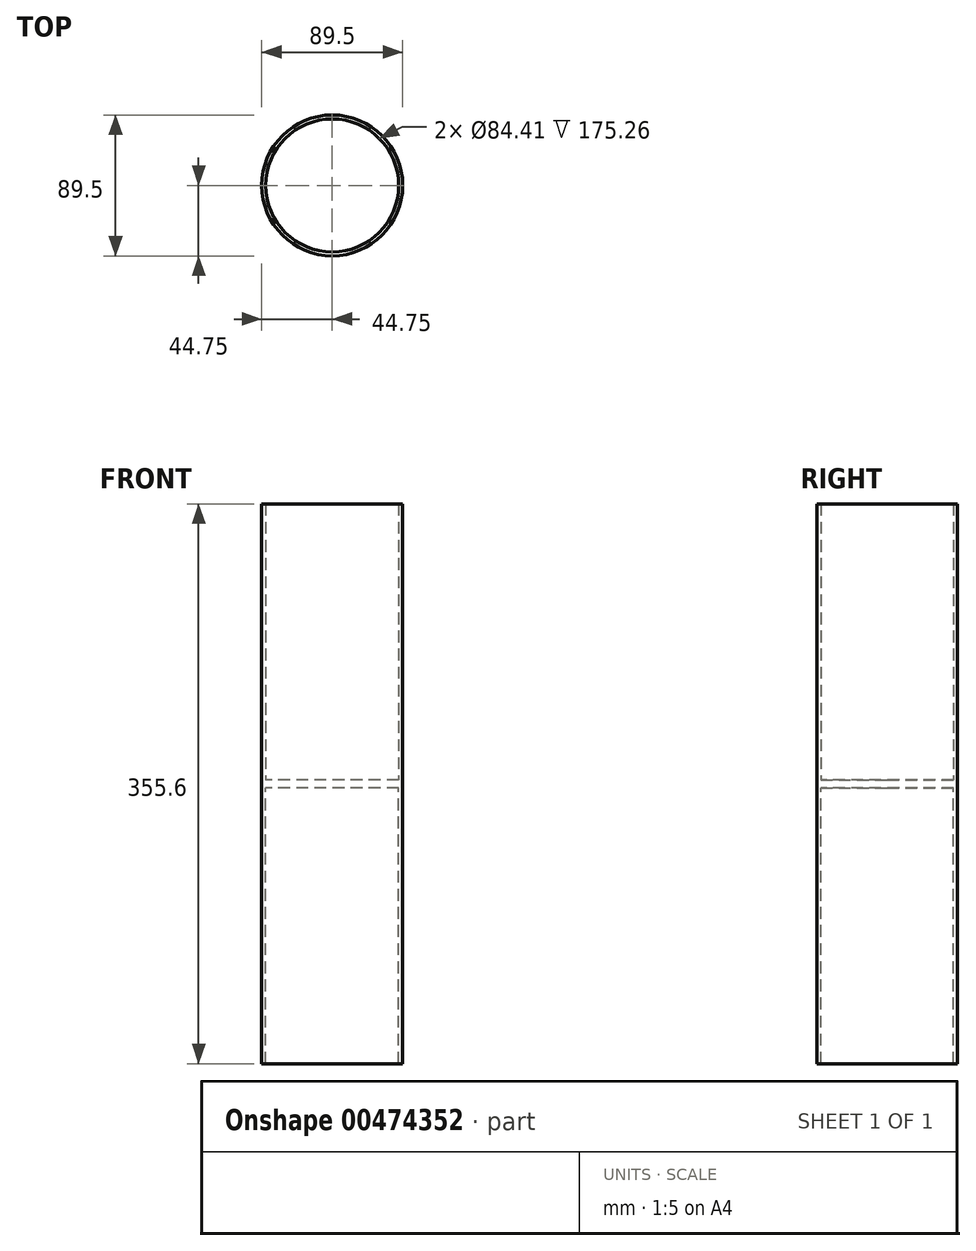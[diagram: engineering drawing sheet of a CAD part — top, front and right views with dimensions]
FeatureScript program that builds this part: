
annotation { "Feature Type Name" : "Feature", "Feature Type Description" : "" }
export const myFeature = defineFeature(function(context is Context, id is Id, definition is map)
    precondition{}
    {
        {
            var Q0;
            Q0=qCreatedBy(makeId("Top.planeOp"),FACE);
            var sketch = newSketch(context, id + "F0", { "sketchPlane" : qUnion([Q0])});
            skCircle(sketch, "E0", {"center": v(0, 0) * mm, "radius": 44.75 * mm});
            skSolve(sketch);
        }
        {
            var Q0;
            Q0 = qSketchRegion(id + "F0", true);
            extrude(context, id + "F1", {"entities" : qUnion([Q0]), "depth" : 177.8 * mm});
        }
        {
            var Q0;
            Q0=makeQuery(id+"F1.opExtrude","CAP_FACE",FACE,{"disambiguationData":[OSD([sQuery(id+"F0.wireOp",EDGE,"E0")])],"isStart":false});
            shell(context, id + "F2", {"entities" : qUnion([Q0]), "thickness" : 2.54 * mm});
        }
        {
            var Q0;
            Q0=makeQuery(id+"F1.opExtrude","SWEPT_BODY",BODY,{"disambiguationData":[OSD([sQuery(id+"F0.wireOp",EDGE,"E0")])]});
            var Q1;
            Q1=qCreatedBy(makeId("Top.planeOp"),FACE);
            mirror(context, id + "F3", {"operationType" : NewBodyOperationType.ADD, "entities" : qUnion([Q0]), "mirrorPlane" : qUnion([Q1])});
        }
    });
